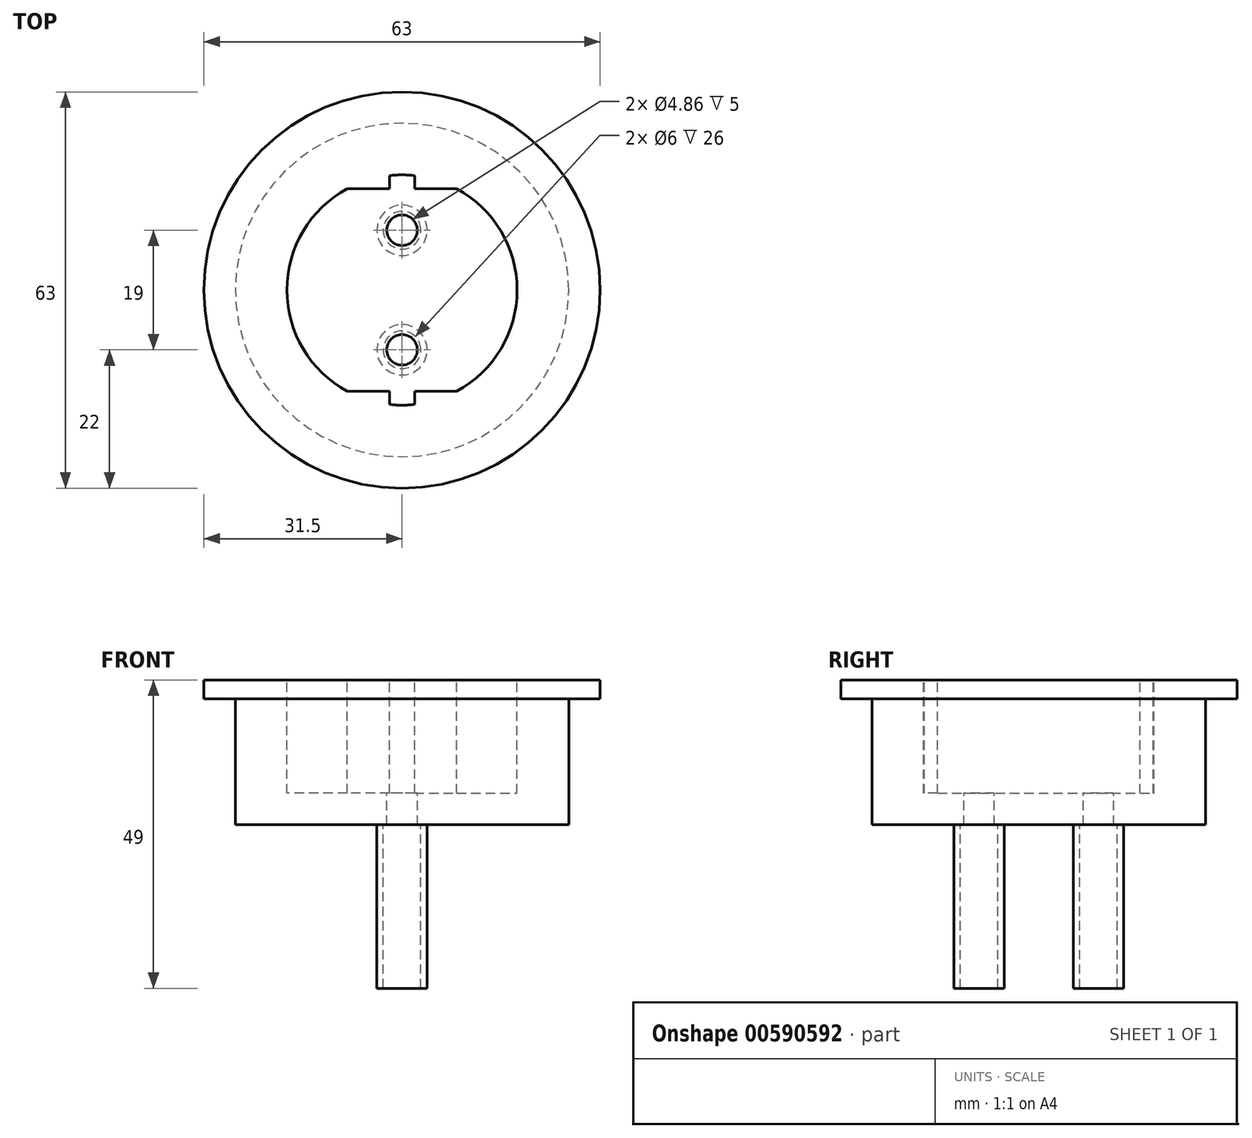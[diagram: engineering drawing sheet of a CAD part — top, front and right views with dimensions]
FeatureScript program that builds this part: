
annotation { "Feature Type Name" : "Feature", "Feature Type Description" : "" }
export const myFeature = defineFeature(function(context is Context, id is Id, definition is map)
    precondition{}
    {
        {
            var Q0;
            Q0=qCreatedBy(makeId("Front.planeOp"),FACE);
            var sketch = newSketch(context, id + "F0", { "sketchPlane" : qUnion([Q0])});
            skLineSegment(sketch, "E0", {"start": v(0, 0) * mm, "end": v(0, 29) * mm});
            skLineSegment(sketch, "E1", {"start": v(0, 29) * mm, "end": v(31.5, 29) * mm});
            skLineSegment(sketch, "E2", {"start": v(31.5, 29) * mm, "end": v(31.5, 26) * mm});
            skLineSegment(sketch, "E3", {"start": v(31.5, 26) * mm, "end": v(26.5, 26) * mm});
            skLineSegment(sketch, "E4", {"start": v(0, 29) * mm, "end": v(0, 6) * mm});
            skLineSegment(sketch, "E5", {"start": v(0, 6) * mm, "end": v(26.5, 6) * mm});
            skPoint(sketch, "E5.endSnap0", {"position": v(26.5, 13) * mm});
            skLineSegment(sketch, "E6", {"start": v(26.5, 26) * mm, "end": v(26.5, 6) * mm});
            skSolve(sketch);
        }
        {
            var Q0;
            Q0=makeQuery(id+"F0.imprint","IMPRINT",FACE,{"disambiguationData":[TD([[makeQuery(id+"F0.imprint","IMPRINT",EDGE,{"derivedFrom":sQuery(id+"F0.wireOp",EDGE,"E1")}),-1.0]])]});
            var Q1;
            Q1=sQuery(id+"F0.wireOp",EDGE,"E0");
            revolve(context, id + "F1", {"entities" : qUnion([Q0]), "axis" : qUnion([Q1]), "revolveType" : RevolveType.FULL});
        }
        {
            var Q0;
            Q0=makeQuery(id+"F1.opRevolve","SWEPT_FACE",FACE,{"disambiguationData":[OSD([sQuery(id+"F0.wireOp",EDGE,"E1")])]});
            var sketch = newSketch(context, id + "F2", { "sketchPlane" : qUnion([Q0])});
            skLineSegment(sketch, "E7", {"start": v(0, 0) * mm, "end": v(18.3, 0) * mm});
            skLineSegment(sketch, "E8", {"start": v(0, 0) * mm, "end": v(0, 16.1) * mm});
            skCircle(sketch, "E9", {"center": v(0, 0) * mm, "radius": 18.3 * mm});
            skLineSegment(sketch, "E10", {"start": v(0, 0) * mm, "end": v(0, -16.1) * mm});
            skLineSegment(sketch, "E11", {"start": v(8.7, 16.1) * mm, "end": v(-8.7, 16.1) * mm});
            skLineSegment(sketch, "E12", {"start": v(0, -16.1) * mm, "end": v(8.7, -16.1) * mm});
            skLineSegment(sketch, "E13", {"start": v(8.7, -16.1) * mm, "end": v(0, -16.1) * mm});
            skLineSegment(sketch, "E14", {"start": v(-8.7, -16.1) * mm, "end": v(0, -16.1) * mm});
            skLineSegment(sketch, "E15", {"start": v(0, 0) * mm, "end": v(0, 9.5) * mm});
            skLineSegment(sketch, "E16", {"start": v(0, 0) * mm, "end": v(0, -9.5) * mm});
            skLineSegment(sketch, "E17", {"start": v(-2, 16.1) * mm, "end": v(2, 16.1) * mm});
            skLineSegment(sketch, "E18", {"start": v(-2, -16.1) * mm, "end": v(2, -16.1) * mm});
            skLineSegment(sketch, "E19", {"start": v(-2, 16.1) * mm, "end": v(-2, 18.2) * mm});
            skLineSegment(sketch, "E20", {"start": v(2, 16.1) * mm, "end": v(2, 18.2) * mm});
            skLineSegment(sketch, "E21", {"start": v(-2, -16.1) * mm, "end": v(-2, -18.2) * mm});
            skLineSegment(sketch, "E22", {"start": v(2, -16.1) * mm, "end": v(2, -18.2) * mm});
            skLineSegment(sketch, "E23", {"start": v(0, 0) * mm, "end": v(10, 0) * mm});
            skSolve(sketch);
        }
        {
            var Q0;
            {var subQ0=sQuery(id+"F2.wireOp",EDGE,"E21");Q0=makeQuery(id+"F2.imprint","IMPRINT",FACE,{"disambiguationData":[TD([[makeQuery(id+"F2.imprint","IMPRINT",EDGE,{"derivedFrom":subQ0}),1.0]])]});}
            var Q1;
            {var subQ7=sQuery(id+"F2.wireOp",EDGE,"E8");Q1=makeQuery(id+"F2.imprint","IMPRINT",FACE,{"disambiguationData":[TD([[makeQuery(id+"F2.imprint","IMPRINT",EDGE,{"derivedFrom":subQ7}),1.0]])]});}
            var Q2;
            {var subQ0=sQuery(id+"F2.wireOp",EDGE,"E19");Q2=makeQuery(id+"F2.imprint","IMPRINT",FACE,{"disambiguationData":[TD([[makeQuery(id+"F2.imprint","IMPRINT",EDGE,{"derivedFrom":subQ0}),-1.0]])]});}
            var Q3;
            {var subQ6=sQuery(id+"F2.wireOp",EDGE,"E7");Q3=makeQuery(id+"F2.imprint","IMPRINT",FACE,{"disambiguationData":[TD([[makeQuery(id+"F2.imprint","IMPRINT",EDGE,{"derivedFrom":subQ6}),1.0]])]});}
            var Q4;
            {var subQ2=sQuery(id+"F2.wireOp",EDGE,"E7");Q4=makeQuery(id+"F2.imprint","IMPRINT",FACE,{"disambiguationData":[TD([[makeQuery(id+"F2.imprint","IMPRINT",EDGE,{"derivedFrom":subQ2}),-1.0]])]});}
            extrude(context, id + "F3", {"entities" : qUnion([Q0, Q1, Q2, Q3, Q4]), "operationType" : NewBodyOperationType.REMOVE, "oppositeDirection" : true, "depth" : 18 * mm, "offsetDistance" : 25 * mm});
        }
        {
            var Q0;
            Q0=sQuery(id+"F2.wireOp",VERTEX,"E15.end");
            var Q1;
            Q1=sQuery(id+"F2.wireOp",VERTEX,"E16.end");
            var Q2;
            Q2=makeQuery(id+"F1.opRevolve","SWEPT_BODY",BODY,{"disambiguationData":[OSD([sQuery(id+"F0.wireOp",EDGE,"E0"),sQuery(id+"F0.wireOp",EDGE,"E1"),sQuery(id+"F0.wireOp",EDGE,"E2"),sQuery(id+"F0.wireOp",EDGE,"E3"),sQuery(id+"F0.wireOp",EDGE,"YAWO67Hd-5U8C-U3rc-iRtI-eKS0pJLDJjBz"),sQuery(id+"F0.wireOp",EDGE,"WrtkL62Z-Nl6X-ohxe-ayLN-IRGdZlgAnF6L")])]});
            hole(context, id + "F4", {"style" : HoleStyle.SIMPLE, "endStyle" : HoleEndStyle.THROUGH, "holeDiameter" : 4.86 * mm, "majorDiameter" : 5 * mm, "isTappedThrough" : true, "tappedDepth" : 12 * mm, "tapClearance" : 3, "locations" : qUnion([Q0, Q1]), "scope" : qUnion([Q2])});
        }
        {
            var Q0;
            Q0=makeQuery(id+"F1.opRevolve","SWEPT_FACE",FACE,{"disambiguationData":[OSD([sQuery(id+"F0.wireOp",EDGE,"E5")])]});
            var sketch = newSketch(context, id + "F5", { "sketchPlane" : qUnion([Q0])});
            skLineSegment(sketch, "E24", {"start": v(0, 9.5) * mm, "end": v(-3, 9.5) * mm});
            skLineSegment(sketch, "E25", {"start": v(-3, 9.5) * mm, "end": v(-4, 9.5) * mm});
            skCircle(sketch, "E26", {"center": v(0, 9.5) * mm, "radius": 3 * mm});
            skCircle(sketch, "E27", {"center": v(0, 9.5) * mm, "radius": 4 * mm});
            skLineSegment(sketch, "E28", {"start": v(0, -9.5) * mm, "end": v(-3, -9.5) * mm});
            skLineSegment(sketch, "E29", {"start": v(-3, -9.5) * mm, "end": v(-4, -9.5) * mm});
            skCircle(sketch, "E30", {"center": v(0, -9.5) * mm, "radius": 3 * mm});
            skCircle(sketch, "E31", {"center": v(0, -9.5) * mm, "radius": 4 * mm});
            skSolve(sketch);
        }
        {
            var Q0;
            Q0 = qSketchRegion(id + "F5", true);
            extrude(context, id + "F6", {"entities" : qUnion([Q0]), "operationType" : NewBodyOperationType.ADD, "depth" : 26 * mm, "offsetDistance" : 25 * mm});
        }
    });
